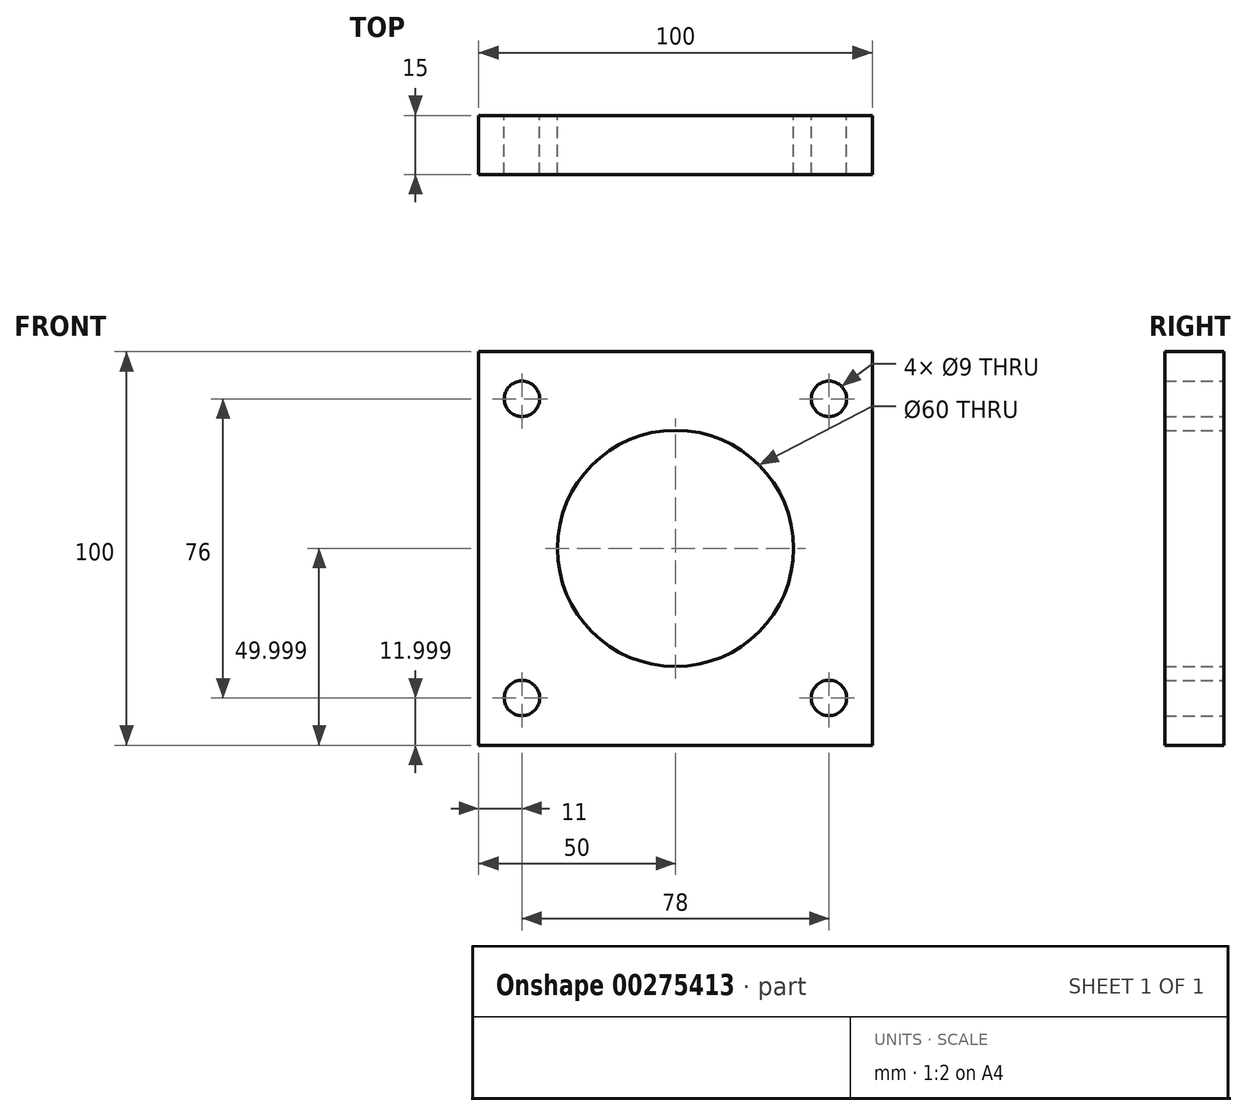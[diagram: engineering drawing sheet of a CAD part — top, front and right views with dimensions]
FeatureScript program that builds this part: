
annotation { "Feature Type Name" : "Feature", "Feature Type Description" : "" }
export const myFeature = defineFeature(function(context is Context, id is Id, definition is map)
    precondition{}
    {
        {
            var Q0;
            Q0=qCreatedBy(makeId("Front.planeOp"),FACE);
            var sketch = newSketch(context, id + "F0", { "sketchPlane" : qUnion([Q0])});
            skLineSegment(sketch, "E0.bottom", {"start": v(-11, 56.03) * mm, "end": v(89, 56.03) * mm});
            skLineSegment(sketch, "E0.top", {"start": v(-11, -43.97) * mm, "end": v(89, -43.97) * mm});
            skLineSegment(sketch, "E0.left", {"start": v(-11, 56.03) * mm, "end": v(-11, -43.97) * mm});
            skLineSegment(sketch, "E0.right", {"start": v(89, 56.03) * mm, "end": v(89, -43.97) * mm});
            skCircle(sketch, "E1", {"center": v(0, 44.03) * mm, "radius": 4.5 * mm});
            skCircle(sketch, "E2", {"center": v(78, 44.03) * mm, "radius": 4.5 * mm});
            skCircle(sketch, "E3", {"center": v(78, -31.97) * mm, "radius": 4.5 * mm});
            skCircle(sketch, "E4", {"center": v(0, -31.97) * mm, "radius": 4.5 * mm});
            skCircle(sketch, "E5", {"center": v(39, 6.03) * mm, "radius": 30 * mm});
            skSolve(sketch);
        }
        {
            var Q0;
            Q0=makeQuery(id+"F0.imprint","IMPRINT",FACE,{"disambiguationData":[TD([[makeQuery(id+"F0.imprint","IMPRINT",EDGE,{"derivedFrom":sQuery(id+"F0.wireOp",EDGE,"E0.bottom")}),-1.0]])]});
            extrude(context, id + "F1", {"entities" : qUnion([Q0]), "depth" : 15 * mm, "offsetDistance" : 25 * mm});
        }
    });
